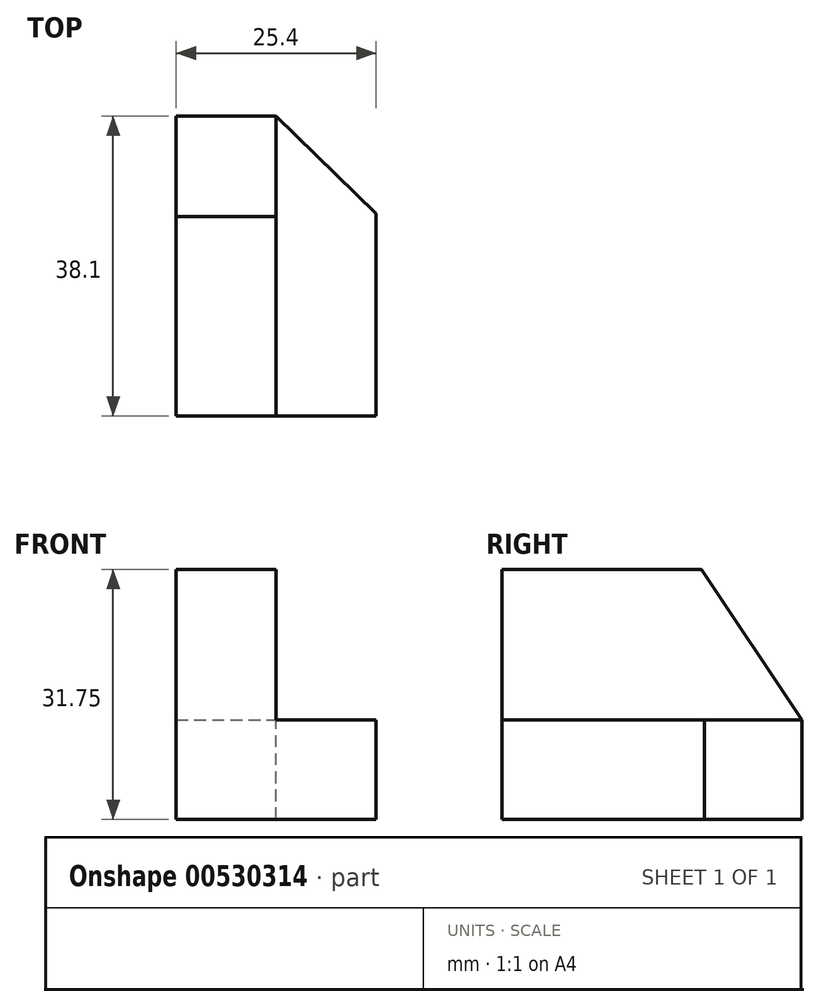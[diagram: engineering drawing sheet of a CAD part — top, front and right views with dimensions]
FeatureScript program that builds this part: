
annotation { "Feature Type Name" : "Feature", "Feature Type Description" : "" }
export const myFeature = defineFeature(function(context is Context, id is Id, definition is map)
    precondition{}
    {
        {
            var Q0;
            Q0=qCreatedBy(makeId("Right.planeOp"),FACE);
            var sketch = newSketch(context, id + "F0", { "sketchPlane" : qUnion([Q0])});
            skLineSegment(sketch, "E0", {"start": v(-63.3, 0) * mm, "end": v(-25.2, 0) * mm});
            skLineSegment(sketch, "E1", {"start": v(-25.2, 0) * mm, "end": v(-25.2, 31.75) * mm});
            skLineSegment(sketch, "E2", {"start": v(-25.2, 31.75) * mm, "end": v(-63.3, 31.75) * mm});
            skLineSegment(sketch, "E3", {"start": v(-63.3, 31.75) * mm, "end": v(-63.3, 0) * mm});
            skLineSegment(sketch, "E4", {"start": v(-63.3, 0) * mm, "end": v(-63.3, 12.66) * mm});
            skLineSegment(sketch, "E5", {"start": v(-63.3, 12.66) * mm, "end": v(-25.2, 12.66) * mm});
            skSolve(sketch);
        }
        {
            var Q0;
            {var subQ0=sQuery(id+"F0.wireOp",EDGE,"E2");Q0=makeQuery(id+"F0.imprint","IMPRINT",FACE,{"disambiguationData":[TD([[makeQuery(id+"F0.imprint","IMPRINT",EDGE,{"derivedFrom":subQ0}),1.0]])]});}
            var Q1;
            {var subQ0=sQuery(id+"F0.wireOp",EDGE,"E0");Q1=makeQuery(id+"F0.imprint","IMPRINT",FACE,{"disambiguationData":[TD([[makeQuery(id+"F0.imprint","IMPRINT",EDGE,{"derivedFrom":subQ0}),1.0]])]});}
            extrude(context, id + "F1", {"entities" : qUnion([Q0, Q1]), "depth" : 25.4 * mm, "offsetDistance" : 25.4 * mm});
        }
        {
            var Q0;
            Q0=makeQuery(id+"F1.opExtrude","CAP_FACE",FACE,{"disambiguationData":[OSD([sQuery(id+"F0.wireOp",EDGE,"E0"),sQuery(id+"F0.wireOp",EDGE,"E1"),sQuery(id+"F0.wireOp",EDGE,"E2"),sQuery(id+"F0.wireOp",EDGE,"E3"),sQuery(id+"F0.wireOp",EDGE,"E4")])],"isStart":false});
            var sketch = newSketch(context, id + "F2", { "sketchPlane" : qUnion([Q0])});
            skLineSegment(sketch, "E6", {"start": v(-63.3, 0) * mm, "end": v(-63.3, 12.66) * mm});
            skLineSegment(sketch, "E7", {"start": v(-63.3, 12.66) * mm, "end": v(-25.2, 12.66) * mm});
            skSolve(sketch);
        }
        {
            var Q0;
            {var subQ0=sQuery(id+"F2.wireOp",EDGE,"E7");Q0=makeQuery(id+"F2.imprint","IMPRINT",FACE,{"disambiguationData":[TD([[makeQuery(id+"F2.imprint","IMPRINT",EDGE,{"derivedFrom":subQ0}),1.0]])]});}
            extrude(context, id + "F3", {"entities" : qUnion([Q0]), "operationType" : NewBodyOperationType.REMOVE, "oppositeDirection" : true, "depth" : 12.7 * mm, "offsetDistance" : 25.4 * mm});
        }
        {
            var Q0;
            Q0=makeQuery(id+"F3.boolean.opBoolean","COPY",FACE,{"derivedFrom":makeQuery(id+"F3.opExtrude","SWEPT_FACE",FACE,{"disambiguationData":[OSD([sQuery(id+"F2.wireOp",EDGE,"E7")])]})});
            var sketch = newSketch(context, id + "F4", { "sketchPlane" : qUnion([Q0])});
            skLineSegment(sketch, "E8", {"start": v(25.4, -25.2) * mm, "end": v(25.4, -37.6) * mm});
            skLineSegment(sketch, "E9", {"start": v(25.4, -25.2) * mm, "end": v(12.7, -25.2) * mm});
            skLineSegment(sketch, "E10", {"start": v(12.7, -25.2) * mm, "end": v(25.4, -37.6) * mm});
            skSolve(sketch);
        }
        {
            var Q0;
            Q0=makeQuery(id+"F4.imprint","IMPRINT",FACE,{"disambiguationData":[TD([[makeQuery(id+"F4.imprint","IMPRINT",EDGE,{"derivedFrom":sQuery(id+"F4.wireOp",EDGE,"E8")}),1.0]])]});
            extrude(context, id + "F5", {"entities" : qUnion([Q0]), "operationType" : NewBodyOperationType.REMOVE, "endBound" : BoundingType.THROUGH_ALL, "oppositeDirection" : true, "depth" : 25.4 * mm, "offsetDistance" : 25.4 * mm});
        }
        {
            var Q0;
            Q0=makeQuery(id+"F3.boolean.opBoolean","COPY",FACE,{"derivedFrom":makeQuery(id+"F3.opExtrude","CAP_FACE",FACE,{"disambiguationData":[OSD([sQuery(id+"F0.wireOp",EDGE,"E1"),sQuery(id+"F0.wireOp",EDGE,"E2"),sQuery(id+"F0.wireOp",EDGE,"E3"),sQuery(id+"F0.wireOp",EDGE,"E4"),sQuery(id+"F2.wireOp",EDGE,"E7")])],"isStart":false})});
            var sketch = newSketch(context, id + "F6", { "sketchPlane" : qUnion([Q0])});
            skLineSegment(sketch, "E11", {"start": v(-25.2, 31.75) * mm, "end": v(-38, 31.75) * mm});
            skLineSegment(sketch, "E12", {"start": v(-38, 31.75) * mm, "end": v(-25.2, 12.66) * mm});
            skSolve(sketch);
        }
        {
            var Q0;
            Q0=makeQuery(id+"F6.imprint","IMPRINT",FACE,{"disambiguationData":[TD([[makeQuery(id+"F6.imprint","IMPRINT",EDGE,{"derivedFrom":sQuery(id+"F6.wireOp",EDGE,"E11")}),1.0]])]});
            extrude(context, id + "F7", {"entities" : qUnion([Q0]), "operationType" : NewBodyOperationType.REMOVE, "endBound" : BoundingType.THROUGH_ALL, "oppositeDirection" : true, "depth" : 25.4 * mm, "offsetDistance" : 25.4 * mm});
        }
    });
